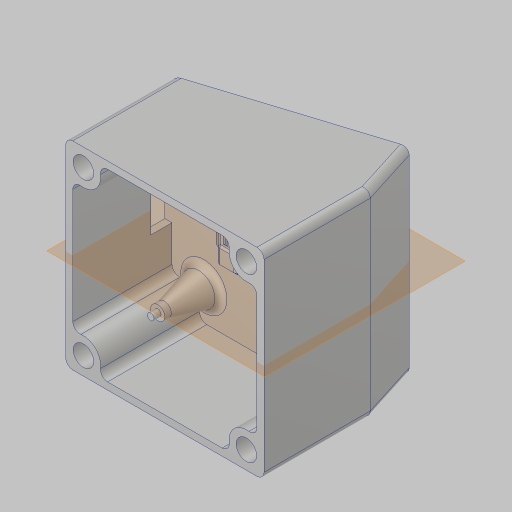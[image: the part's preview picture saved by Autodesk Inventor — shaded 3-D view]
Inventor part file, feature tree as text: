
AUTODESK INVENTOR PART (.ipt)
format: ipt  version: 2023.5 (Build 275446000, 446)  size: 446,976 bytes
history: native  units: in
note: dims shown in document units (in); Inventor stores cm internally (conversion verified against a paired STEP export)
features: extrude x8, projected_geometry x4, fillet x2, chamfer x2, hole x1, mirror x1, shell x1, plane x1
ambient origin geometry x8: Origin, YZ Plane, XZ Plane, XY Plane, X Axis, Y Axis, Z Axis, Center Point
bodies: Solid1 (feature_tree)
feature tree (20):
  extrude  "Extrusion1"  Depth=1.4961in
  hole  "Hole1"  [1 undecoded]
  extrude  "Extrusion6"  Depth=1.3386in
  mirror  "Mirror1"
  shell  "Shell1"  Thickness=1.3386in
  extrude  "Extrusion7"  Depth=1.1811in TaperAngle=0.0deg
  fillet  "Fillet1"  Radius=0.0787in
  extrude  "Extrusion2"  Depth=0.3937in
  chamfer  "Chamfer1"  Distance=1.811in
  extrude  "Extrusion3"  Depth=0.0787in
  extrude  "Extrusion4"  Depth=0.1575in
  plane  "Work Plane1"
  extrude  "Extrusion5"  Depth=0.1575in
  chamfer  "Chamfer2"  Distance=0.1575in
  fillet  "Fillet3"  Radius=0.1575in
  extrude  "Extrusion8"  Depth=0.5906in TaperAngle=0.0deg
  projected_geometry  "Projected Loop1"
  projected_geometry  "Projected Loop2"
  projected_geometry  "Projected Loop3"
  projected_geometry  "Project Cut Edges1"
note: 1 required parameter value undecoded (feature->parameter linkage not recoverable at this tier; creation-order binding heuristic only, values carry confidence <= 0.55)
